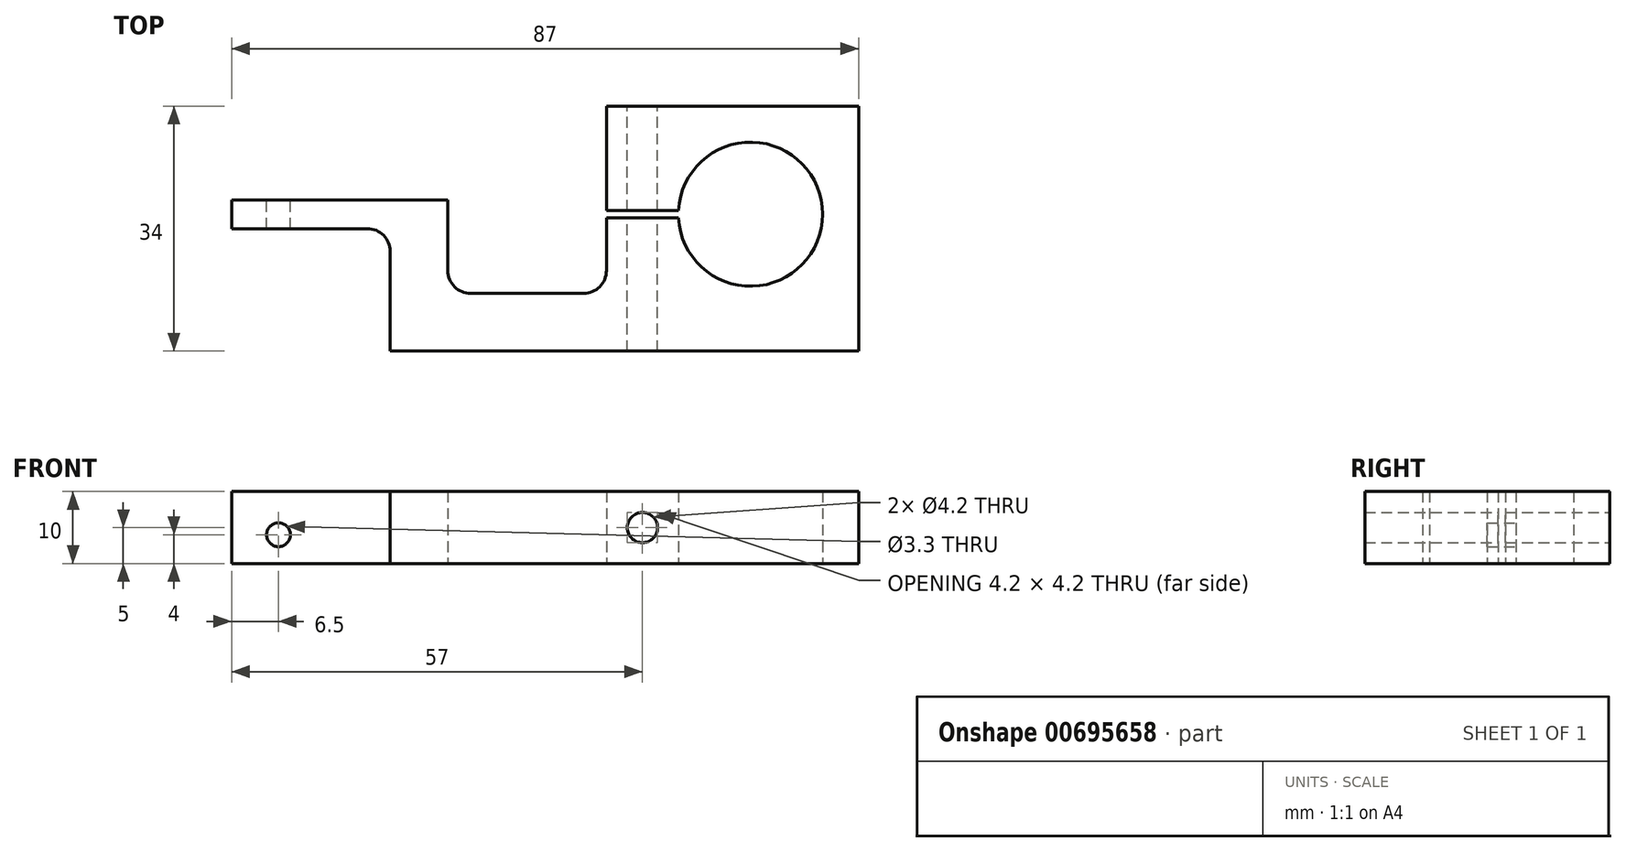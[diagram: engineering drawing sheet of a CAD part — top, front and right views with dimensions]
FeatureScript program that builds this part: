
annotation { "Feature Type Name" : "Feature", "Feature Type Description" : "" }
export const myFeature = defineFeature(function(context is Context, id is Id, definition is map)
    precondition{}
    {
        {
            var Q0;
            Q0=qCreatedBy(makeId("Top.planeOp"),FACE);
            var sketch = newSketch(context, id + "F0", { "sketchPlane" : qUnion([Q0])});
            skArc(sketch, "E0", {"start": v(-9.99, -0.5) * mm, "mid": v(10, 0) * mm, "end": v(-9.99, 0.5) * mm});
            skLineSegment(sketch, "E1.bottom", {"start": v(-20, 15) * mm, "end": v(15, 15) * mm});
            skLineSegment(sketch, "E1.top", {"start": v(-50, -19) * mm, "end": v(15, -19) * mm});
            skLineSegment(sketch, "E1.right", {"start": v(15, 15) * mm, "end": v(15, -19) * mm});
            skLineSegment(sketch, "E2", {"start": v(-50, -19) * mm, "end": v(-50, -5.18) * mm});
            skLineSegment(sketch, "E3", {"start": v(-53.18, -2) * mm, "end": v(-72, -2) * mm});
            skLineSegment(sketch, "E4", {"start": v(-72, -2) * mm, "end": v(-72, 2) * mm});
            skLineSegment(sketch, "E5", {"start": v(-72, 2) * mm, "end": v(-42, 2) * mm});
            skLineSegment(sketch, "E6", {"start": v(-42, 2) * mm, "end": v(-42, -7.83) * mm});
            skLineSegment(sketch, "E7", {"start": v(-38.83, -11) * mm, "end": v(-23.18, -11) * mm});
            skLineSegment(sketch, "E8", {"start": v(-20, -7.83) * mm, "end": v(-20, -0.5) * mm});
            skPoint(sketch, "E9.visualSharp", {"position": v(-50, -2) * mm});
            skArc(sketch, "E9.filletArc", {"start": v(-50, -5.18) * mm, "mid": v(-50.93, -2.93) * mm, "end": v(-53.18, -2) * mm});
            skPoint(sketch, "E10.visualSharp", {"position": v(-42, -11) * mm});
            skArc(sketch, "E10.filletArc", {"start": v(-42, -7.83) * mm, "mid": v(-41.07, -10.07) * mm, "end": v(-38.83, -11) * mm});
            skPoint(sketch, "E11.visualSharp", {"position": v(-20, -11) * mm});
            skArc(sketch, "E11.filletArc", {"start": v(-23.18, -11) * mm, "mid": v(-20.93, -10.07) * mm, "end": v(-20, -7.83) * mm});
            skLineSegment(sketch, "E12", {"start": v(0, 0) * mm, "end": v(-26.04, 0) * mm, "construction": true});
            skLineSegment(sketch, "E13.bottom", {"start": v(-9.99, -0.5) * mm, "end": v(-20, -0.5) * mm});
            skLineSegment(sketch, "E13.top", {"start": v(-9.99, 0.5) * mm, "end": v(-20, 0.5) * mm});
            skPoint(sketch, "E13.middle", {"position": v(-15.26, 0) * mm});
            skPoint(sketch, "E14.orphan", {"position": v(-22.24, -0.5) * mm});
            skPoint(sketch, "E13.right.end.orphan", {"position": v(-22.24, 0.5) * mm});
            skPoint(sketch, "E15.orphan", {"position": v(-8.28, -0.5) * mm});
            skPoint(sketch, "E16.orphan", {"position": v(-8.28, 0.5) * mm});
            skLineSegment(sketch, "E17.trimOffspring", {"start": v(-20, 0.5) * mm, "end": v(-20, 15) * mm});
            skSolve(sketch);
        }
        {
            var Q0;
            Q0 = qSketchRegion(id + "F0", true);
            extrude(context, id + "F1", {"entities" : qUnion([Q0]), "depth" : 10 * mm, "offsetDistance" : 25 * mm});
        }
        {
            var Q0;
            Q0=makeQuery(id+"F1.opExtrude","SWEPT_FACE",FACE,{"disambiguationData":[OSD([sQuery(id+"F0.wireOp",EDGE,"E1.bottom")])]});
            var sketch = newSketch(context, id + "F2", { "sketchPlane" : qUnion([Q0])});
            skLineSegment(sketch, "E18", {"start": v(20, 5) * mm, "end": v(-15, 5) * mm, "construction": true});
            skLineSegment(sketch, "E19", {"start": v(15, 10) * mm, "end": v(15, 0) * mm, "construction": true});
            skPoint(sketch, "E20", {"position": v(15, 5) * mm});
            skSolve(sketch);
        }
        {
            var Q0;
            Q0=sQuery(id+"F2.wireOp",VERTEX,"E20");
            var Q1;
            Q1=makeQuery(id+"F1.opExtrude","SWEPT_BODY",BODY,{"disambiguationData":[OSD([sQuery(id+"F0.wireOp",EDGE,"E0"),sQuery(id+"F0.wireOp",EDGE,"E1.bottom"),sQuery(id+"F0.wireOp",EDGE,"E1.top"),sQuery(id+"F0.wireOp",EDGE,"E1.right"),sQuery(id+"F0.wireOp",EDGE,"E2"),sQuery(id+"F0.wireOp",EDGE,"E3"),sQuery(id+"F0.wireOp",EDGE,"E4"),sQuery(id+"F0.wireOp",EDGE,"E5"),sQuery(id+"F0.wireOp",EDGE,"E6"),sQuery(id+"F0.wireOp",EDGE,"E7"),sQuery(id+"F0.wireOp",EDGE,"E8"),sQuery(id+"F0.wireOp",EDGE,"E9.filletArc"),sQuery(id+"F0.wireOp",EDGE,"E10.filletArc"),sQuery(id+"F0.wireOp",EDGE,"E11.filletArc")])]});
            hole(context, id + "F3", {"style" : HoleStyle.SIMPLE, "endStyle" : HoleEndStyle.THROUGH, "standardTappedOrClearance" : lookupTablePath({ "standard" : "ISO", "engagement" : "75%", "pitch" : "0.8 mm", "size" : "M5", "type" : "Tapped" }), "standardBlindInLast" : lookupTablePath({ "standard" : "ISO", "engagement" : "75%", "pitch" : "0.8 mm", "size" : "M5", "type" : "Tapped" }), "holeDiameter" : 4.2 * mm, "majorDiameter" : 5 * mm, "showTappedDepth" : true, "isTappedThrough" : true, "tappedDepth" : 12 * mm, "tapClearance" : 3, "locations" : qUnion([Q0]), "scope" : qUnion([Q1])});
        }
        {
            var Q0;
            Q0=makeQuery(id+"F1.opExtrude","SWEPT_FACE",FACE,{"disambiguationData":[OSD([sQuery(id+"F0.wireOp",EDGE,"E5")])]});
            var sketch = newSketch(context, id + "F4", { "sketchPlane" : qUnion([Q0])});
            skLineSegment(sketch, "E21", {"start": v(72, 4) * mm, "end": v(42, 4) * mm, "construction": true});
            skPoint(sketch, "E22", {"position": v(65.5, 4) * mm});
            skSolve(sketch);
        }
        {
            var Q0;
            Q0=sQuery(id+"F4.wireOp",VERTEX,"E22");
            var Q1;
            Q1=makeQuery(id+"F1.opExtrude","SWEPT_BODY",BODY,{"disambiguationData":[OSD([sQuery(id+"F0.wireOp",EDGE,"E0"),sQuery(id+"F0.wireOp",EDGE,"E1.bottom"),sQuery(id+"F0.wireOp",EDGE,"E1.top"),sQuery(id+"F0.wireOp",EDGE,"E1.right"),sQuery(id+"F0.wireOp",EDGE,"E2"),sQuery(id+"F0.wireOp",EDGE,"E3"),sQuery(id+"F0.wireOp",EDGE,"E4"),sQuery(id+"F0.wireOp",EDGE,"E5"),sQuery(id+"F0.wireOp",EDGE,"E6"),sQuery(id+"F0.wireOp",EDGE,"E7"),sQuery(id+"F0.wireOp",EDGE,"E8"),sQuery(id+"F0.wireOp",EDGE,"E9.filletArc"),sQuery(id+"F0.wireOp",EDGE,"E10.filletArc"),sQuery(id+"F0.wireOp",EDGE,"E11.filletArc"),sQuery(id+"F0.wireOp",EDGE,"E13.bottom"),sQuery(id+"F0.wireOp",EDGE,"E13.top"),sQuery(id+"F0.wireOp",EDGE,"E17.trimOffspring")])]});
            hole(context, id + "F5", {"style" : HoleStyle.SIMPLE, "endStyle" : HoleEndStyle.THROUGH, "standardTappedOrClearance" : lookupTablePath({ "standard" : "ISO", "fit" : "Normal", "size" : "M3", "type" : "Clearance" }), "standardBlindInLast" : lookupTablePath({ "fit" : "Standard", "standard" : "ISO", "size" : "M3", "type" : "Clearance" }), "holeDiameter" : 3.3 * mm, "majorDiameter" : 5 * mm, "isTappedThrough" : true, "tappedDepth" : 12 * mm, "tapClearance" : 3, "locations" : qUnion([Q0]), "scope" : qUnion([Q1])});
        }
    });
